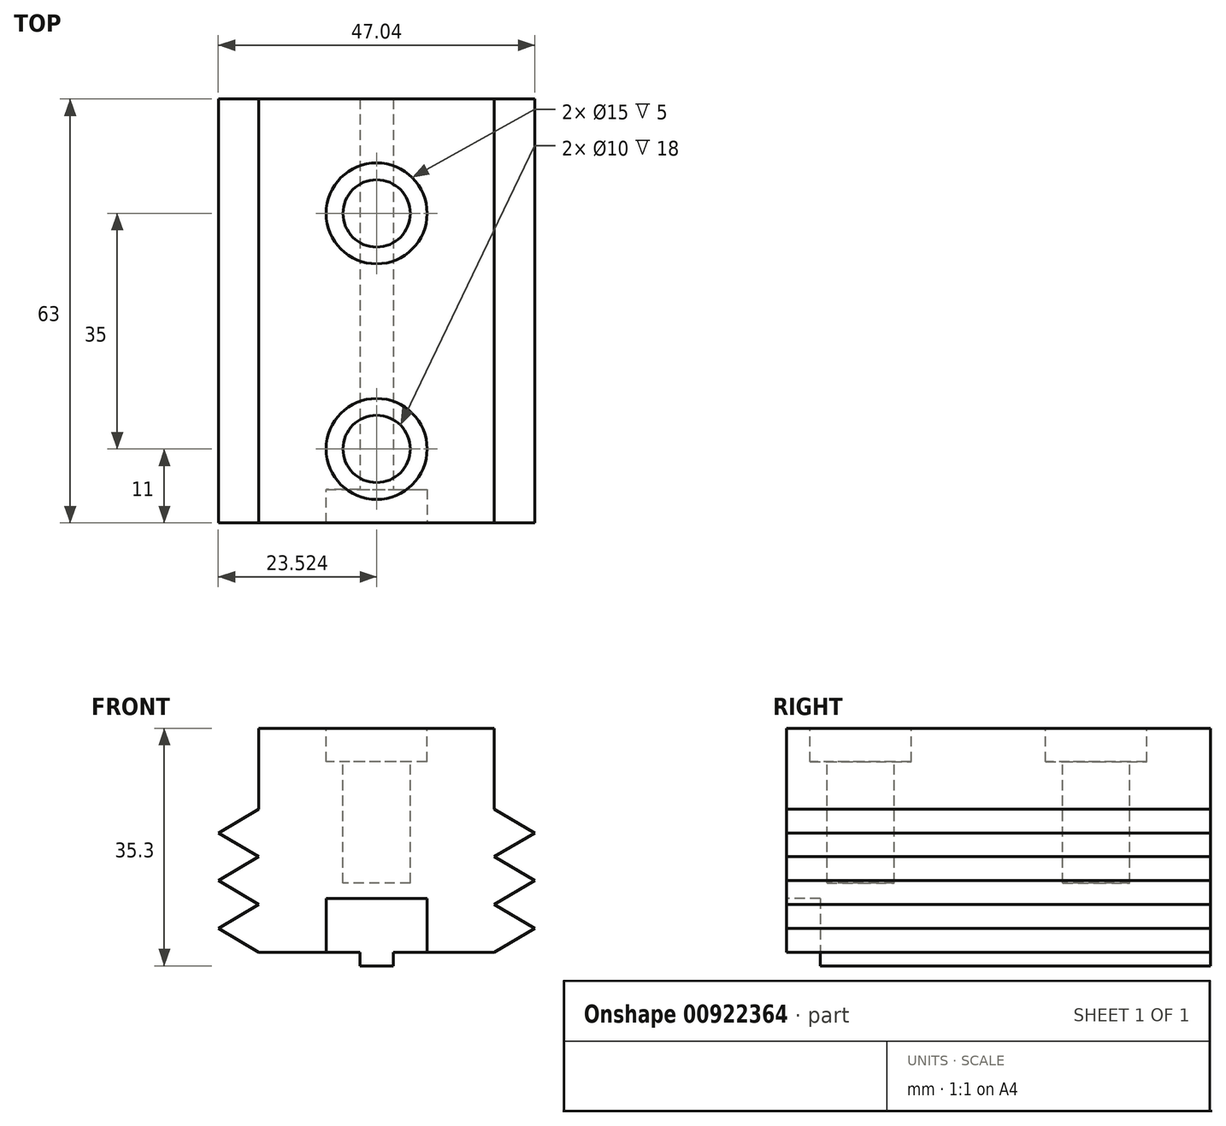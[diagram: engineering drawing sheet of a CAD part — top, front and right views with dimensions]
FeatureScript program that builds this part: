
annotation { "Feature Type Name" : "Feature", "Feature Type Description" : "" }
export const myFeature = defineFeature(function(context is Context, id is Id, definition is map)
    precondition{}
    {
        {
            var Q0;
            Q0=qCreatedBy(makeId("Top.planeOp"),FACE);
            var sketch = newSketch(context, id + "F0", { "sketchPlane" : qUnion([Q0])});
            skLineSegment(sketch, "E0.bottom", {"start": v(-17.99, 0) * mm, "end": v(17.01, 0) * mm});
            skLineSegment(sketch, "E0.top", {"start": v(-17.99, -63) * mm, "end": v(17.01, -63) * mm});
            skLineSegment(sketch, "E0.left", {"start": v(-17.99, 0) * mm, "end": v(-17.99, -63) * mm});
            skLineSegment(sketch, "E0.right", {"start": v(17.01, 0) * mm, "end": v(17.01, -63) * mm});
            skSolve(sketch);
        }
        {
            var Q0;
            Q0=makeQuery(id+"F0.imprint","IMPRINT",FACE,{"disambiguationData":[TD([[makeQuery(id+"F0.imprint","IMPRINT",EDGE,{"derivedFrom":sQuery(id+"F0.wireOp",EDGE,"E0.bottom")}),-1.0]])]});
            extrude(context, id + "F1", {"entities" : qUnion([Q0]), "oppositeDirection" : true, "depth" : 35.3 * mm, "offsetDistance" : 25 * mm});
        }
        {
            var Q0;
            Q0=makeQuery(id+"F1.opExtrude","SWEPT_FACE",FACE,{"disambiguationData":[OSD([sQuery(id+"F0.wireOp",EDGE,"E0.top")])]});
            var sketch = newSketch(context, id + "F2", { "sketchPlane" : qUnion([Q0])});
            skLineSegment(sketch, "E1", {"start": v(-17.99, -12) * mm, "end": v(-24, -15.55) * mm});
            skLineSegment(sketch, "E2", {"start": v(-24, -15.55) * mm, "end": v(-17.99, -19.1) * mm});
            skLineSegment(sketch, "E3", {"start": v(-17.99, -19.1) * mm, "end": v(-24, -22.65) * mm});
            skLineSegment(sketch, "E4", {"start": v(-24, -22.65) * mm, "end": v(-17.99, -26.2) * mm});
            skLineSegment(sketch, "E5", {"start": v(-17.99, -26.2) * mm, "end": v(-24, -29.75) * mm});
            skLineSegment(sketch, "E6", {"start": v(-24, -29.75) * mm, "end": v(-17.99, -33.3) * mm});
            skLineSegment(sketch, "E7", {"start": v(17.01, -33.3) * mm, "end": v(23.03, -29.75) * mm});
            skLineSegment(sketch, "E8", {"start": v(23.03, -29.75) * mm, "end": v(17.01, -26.2) * mm});
            skLineSegment(sketch, "E9", {"start": v(17.01, -26.2) * mm, "end": v(23.03, -22.65) * mm});
            skLineSegment(sketch, "E10", {"start": v(23.03, -22.65) * mm, "end": v(17.01, -19.1) * mm});
            skLineSegment(sketch, "E11", {"start": v(17.01, -19.1) * mm, "end": v(23.03, -15.55) * mm});
            skLineSegment(sketch, "E12", {"start": v(23.03, -15.55) * mm, "end": v(17.01, -12) * mm});
            skLineSegment(sketch, "E13", {"start": v(-17.99, -33.3) * mm, "end": v(-2.99, -33.3) * mm});
            skLineSegment(sketch, "E14", {"start": v(17.01, -33.3) * mm, "end": v(2.01, -33.3) * mm});
            skLineSegment(sketch, "E15", {"start": v(-2.99, -33.3) * mm, "end": v(-2.99, -35.3) * mm});
            skLineSegment(sketch, "E16", {"start": v(2.01, -33.3) * mm, "end": v(2.01, -35.3) * mm});
            skLineSegment(sketch, "E17", {"start": v(2.01, -35.3) * mm, "end": v(-2.99, -35.3) * mm});
            skLineSegment(sketch, "E18", {"start": v(-17.99, 0) * mm, "end": v(-17.99, -12) * mm});
            skLineSegment(sketch, "E19", {"start": v(17.01, 0) * mm, "end": v(17.01, -12) * mm});
            skSolve(sketch);
        }
        {
            var Q0;
            Q0=qSketchRegion(id+"F2",true);
            var Q1;
            {var subQ0=sQuery(id+"F2.wireOp",EDGE,"E14");Q1=makeQuery(id+"F2.imprint","IMPRINT",FACE,{"disambiguationData":[TD([[makeQuery(id+"F2.imprint","IMPRINT",EDGE,{"derivedFrom":subQ0}),1.0]])]});}
            var Q2;
            {var subQ0=sQuery(id+"F2.wireOp",EDGE,"E13");Q2=makeQuery(id+"F2.imprint","IMPRINT",FACE,{"disambiguationData":[TD([[makeQuery(id+"F2.imprint","IMPRINT",EDGE,{"derivedFrom":subQ0}),-1.0]])]});}
            extrude(context, id + "F3", {"entities" : qUnion([Q0, Q1, Q2]), "operationType" : NewBodyOperationType.REMOVE, "endBound" : BoundingType.THROUGH_ALL, "oppositeDirection" : true, "depth" : 25 * mm, "offsetDistance" : 25 * mm});
        }
        {
            var Q0;
            {var subQ0=sQuery(id+"F2.wireOp",EDGE,"E1");Q0=makeQuery(id+"F2.imprint","IMPRINT",FACE,{"disambiguationData":[TD([[makeQuery(id+"F2.imprint","IMPRINT",EDGE,{"derivedFrom":subQ0}),1.0]])]});}
            var Q1;
            {var subQ0=sQuery(id+"F2.wireOp",EDGE,"E3");Q1=makeQuery(id+"F2.imprint","IMPRINT",FACE,{"disambiguationData":[TD([[makeQuery(id+"F2.imprint","IMPRINT",EDGE,{"derivedFrom":subQ0}),1.0]])]});}
            var Q2;
            {var subQ0=sQuery(id+"F2.wireOp",EDGE,"E5");Q2=makeQuery(id+"F2.imprint","IMPRINT",FACE,{"disambiguationData":[TD([[makeQuery(id+"F2.imprint","IMPRINT",EDGE,{"derivedFrom":subQ0}),1.0]])]});}
            var Q3;
            {var subQ0=sQuery(id+"F2.wireOp",EDGE,"E7");Q3=makeQuery(id+"F2.imprint","IMPRINT",FACE,{"disambiguationData":[TD([[makeQuery(id+"F2.imprint","IMPRINT",EDGE,{"derivedFrom":subQ0}),1.0]])]});}
            var Q4;
            {var subQ0=sQuery(id+"F2.wireOp",EDGE,"E11");Q4=makeQuery(id+"F2.imprint","IMPRINT",FACE,{"disambiguationData":[TD([[makeQuery(id+"F2.imprint","IMPRINT",EDGE,{"derivedFrom":subQ0}),1.0]])]});}
            var Q5;
            {var subQ0=sQuery(id+"F2.wireOp",EDGE,"E9");Q5=makeQuery(id+"F2.imprint","IMPRINT",FACE,{"disambiguationData":[TD([[makeQuery(id+"F2.imprint","IMPRINT",EDGE,{"derivedFrom":subQ0}),1.0]])]});}
            extrude(context, id + "F4", {"entities" : qUnion([Q0, Q1, Q2, Q3, Q4, Q5]), "operationType" : NewBodyOperationType.ADD, "oppositeDirection" : true, "depth" : 63 * mm, "offsetDistance" : 25 * mm});
        }
        {
            var Q0;
            Q0=makeQuery(id+"F1.opExtrude","CAP_FACE",FACE,{"disambiguationData":[OSD([sQuery(id+"F0.wireOp",EDGE,"E0.bottom"),sQuery(id+"F0.wireOp",EDGE,"E0.top"),sQuery(id+"F0.wireOp",EDGE,"E0.left"),sQuery(id+"F0.wireOp",EDGE,"E0.right")])],"isStart":true});
            var sketch = newSketch(context, id + "F5", { "sketchPlane" : qUnion([Q0])});
            skCircle(sketch, "E20", {"center": v(-0.49, -52) * mm, "radius": 5 * mm});
            skCircle(sketch, "E21", {"center": v(-0.49, -17) * mm, "radius": 5 * mm});
            skCircle(sketch, "E22", {"center": v(-0.49, -17) * mm, "radius": 7.5 * mm});
            skCircle(sketch, "E23", {"center": v(-0.49, -52) * mm, "radius": 7.5 * mm});
            skSolve(sketch);
        }
        {
            var Q0;
            Q0=makeQuery(id+"F5.imprint","IMPRINT",FACE,{"disambiguationData":[TD([[makeQuery(id+"F5.imprint","IMPRINT",EDGE,{"derivedFrom":sQuery(id+"F5.wireOp",EDGE,"E21")}),1.0]])]});
            var Q1;
            Q1=makeQuery(id+"F5.imprint","IMPRINT",FACE,{"disambiguationData":[TD([[makeQuery(id+"F5.imprint","IMPRINT",EDGE,{"derivedFrom":sQuery(id+"F5.wireOp",EDGE,"E20")}),1.0]])]});
            extrude(context, id + "F6", {"entities" : qUnion([Q0, Q1]), "operationType" : NewBodyOperationType.REMOVE, "oppositeDirection" : true, "depth" : 23 * mm, "offsetDistance" : 25 * mm});
        }
        {
            var Q0;
            Q0=qSketchRegion(id+"F5",true);
            extrude(context, id + "F7", {"entities" : qUnion([Q0]), "operationType" : NewBodyOperationType.REMOVE, "oppositeDirection" : true, "depth" : 5 * mm, "offsetDistance" : 25 * mm});
        }
        {
            var Q0;
            {var subQ0=sQuery(id+"F0.wireOp",EDGE,"E0.right");var subQ1=sQuery(id+"F0.wireOp",EDGE,"E0.top");var subQ2=sQuery(id+"F0.wireOp",EDGE,"E0.left");Q0=makeQuery(id+"F4.boolean.opBoolean","MERGE",FACE,{"derivedFrom":[makeQuery(id+"F1.opExtrude","SWEPT_FACE",FACE,{"disambiguationData":[OSD([subQ1])]}),makeQuery(id+"F4.opExtrude","CAP_FACE",FACE,{"disambiguationData":[OSD([subQ1,subQ2,sQuery(id+"F2.wireOp",EDGE,"E1"),sQuery(id+"F2.wireOp",EDGE,"E2")])],"isStart":true}),makeQuery(id+"F4.opExtrude","CAP_FACE",FACE,{"disambiguationData":[OSD([subQ1,subQ2,sQuery(id+"F2.wireOp",EDGE,"E3"),sQuery(id+"F2.wireOp",EDGE,"E4")])],"isStart":true}),makeQuery(id+"F4.opExtrude","CAP_FACE",FACE,{"disambiguationData":[OSD([subQ1,subQ2,sQuery(id+"F2.wireOp",EDGE,"E5"),sQuery(id+"F2.wireOp",EDGE,"E6")])],"isStart":true}),makeQuery(id+"F4.opExtrude","CAP_FACE",FACE,{"disambiguationData":[OSD([subQ1,subQ0,sQuery(id+"F2.wireOp",EDGE,"E7"),sQuery(id+"F2.wireOp",EDGE,"E8")])],"isStart":true}),makeQuery(id+"F4.opExtrude","CAP_FACE",FACE,{"disambiguationData":[OSD([subQ1,subQ0,sQuery(id+"F2.wireOp",EDGE,"E9"),sQuery(id+"F2.wireOp",EDGE,"E10")])],"isStart":true}),makeQuery(id+"F4.opExtrude","CAP_FACE",FACE,{"disambiguationData":[OSD([subQ1,subQ0,sQuery(id+"F2.wireOp",EDGE,"E11"),sQuery(id+"F2.wireOp",EDGE,"E12")])],"isStart":true})]});}
            var sketch = newSketch(context, id + "F8", { "sketchPlane" : qUnion([Q0])});
            skLineSegment(sketch, "E24", {"start": v(-0.49, -35.3) * mm, "end": v(-0.49, -22.62) * mm});
            skLineSegment(sketch, "E25.bottom", {"start": v(-7.99, -25.3) * mm, "end": v(7.01, -25.3) * mm});
            skLineSegment(sketch, "E25.top", {"start": v(-7.99, -35.5) * mm, "end": v(7.01, -35.5) * mm});
            skLineSegment(sketch, "E25.left", {"start": v(-7.99, -25.3) * mm, "end": v(-7.99, -35.5) * mm});
            skLineSegment(sketch, "E25.right", {"start": v(7.01, -25.3) * mm, "end": v(7.01, -35.5) * mm});
            skSolve(sketch);
        }
        {
            var Q0;
            Q0=qSketchRegion(id+"F8",true);
            extrude(context, id + "F9", {"entities" : qUnion([Q0]), "operationType" : NewBodyOperationType.REMOVE, "oppositeDirection" : true, "depth" : 5 * mm, "offsetDistance" : 25 * mm});
        }
    });
